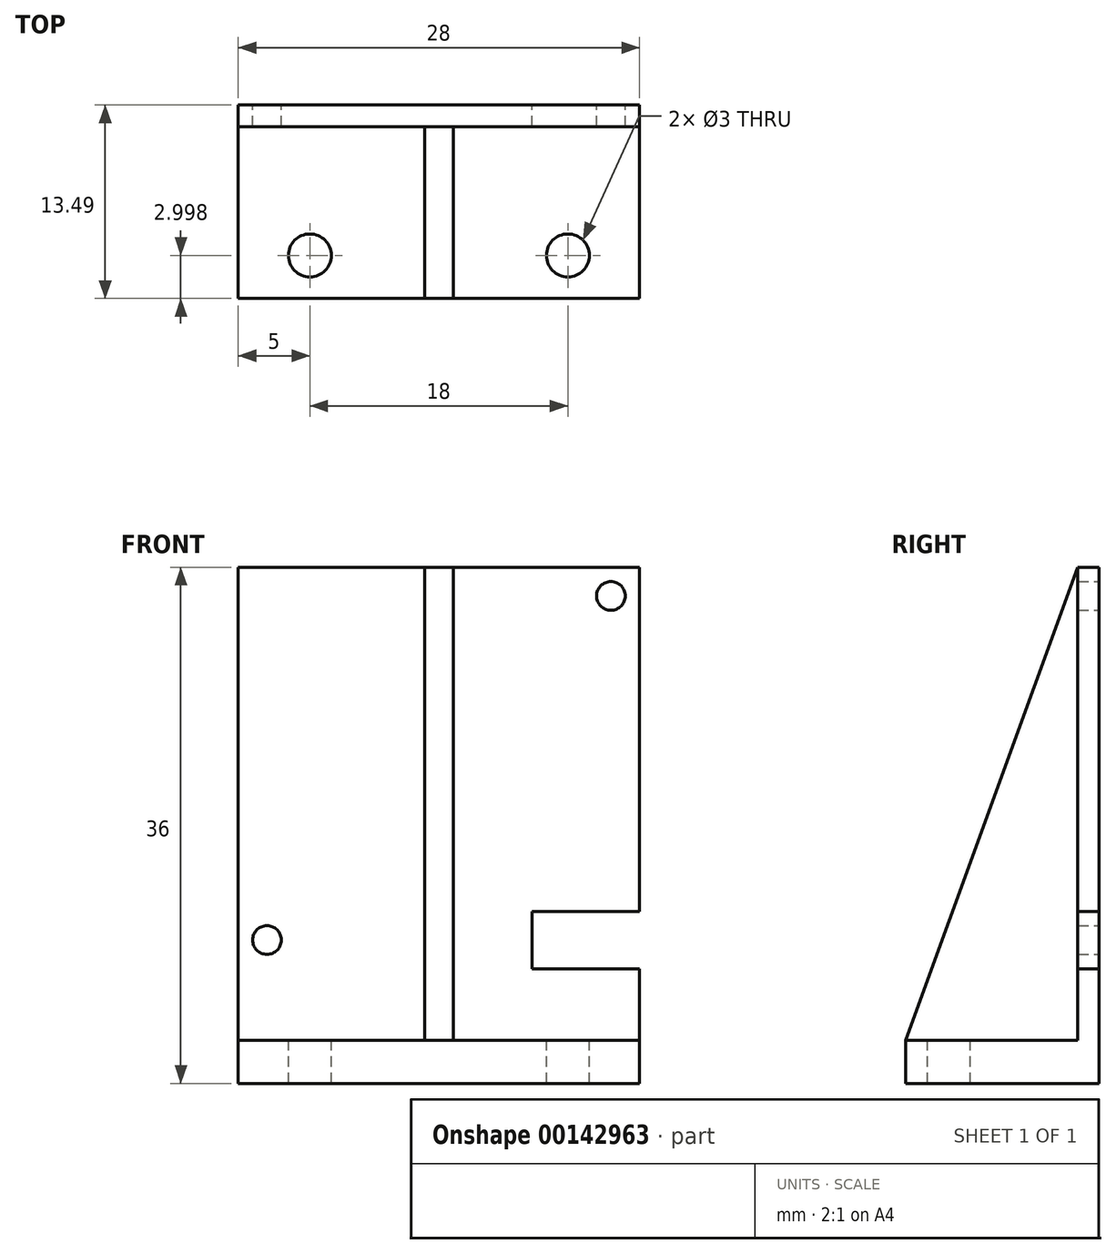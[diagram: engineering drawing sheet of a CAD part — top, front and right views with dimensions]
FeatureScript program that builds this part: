
annotation { "Feature Type Name" : "Feature", "Feature Type Description" : "" }
export const myFeature = defineFeature(function(context is Context, id is Id, definition is map)
    precondition{}
    {
        {
            var Q0;
            Q0=qCreatedBy(makeId("Front.planeOp"),FACE);
            var sketch = newSketch(context, id + "F0", { "sketchPlane" : qUnion([Q0])});
            skLineSegment(sketch, "E0.bottom", {"start": v(14, 16.5) * mm, "end": v(-14, 16.5) * mm});
            skLineSegment(sketch, "E0.top", {"start": v(14, -16.5) * mm, "end": v(-14, -16.5) * mm});
            skLineSegment(sketch, "E0.left", {"start": v(14, 16.5) * mm, "end": v(14, -7.5) * mm});
            skLineSegment(sketch, "E0.right", {"start": v(-14, 16.5) * mm, "end": v(-14, -16.5) * mm});
            skPoint(sketch, "E0.middle", {"position": v(0, 0) * mm});
            skLineSegment(sketch, "E1.bottom", {"start": v(14, -16.5) * mm, "end": v(6.5, -16.5) * mm});
            skLineSegment(sketch, "E1.top", {"start": v(14, -7.5) * mm, "end": v(6.5, -7.5) * mm});
            skLineSegment(sketch, "E1.left", {"start": v(14, -16.5) * mm, "end": v(14, -11.5) * mm});
            skLineSegment(sketch, "E1.right", {"start": v(6.5, -11.5) * mm, "end": v(6.5, -7.5) * mm});
            skLineSegment(sketch, "E2", {"start": v(6.5, -11.5) * mm, "end": v(14, -11.5) * mm});
            skPoint(sketch, "E3.orphan", {"position": v(-14, -11.5) * mm});
            skLineSegment(sketch, "E4.trimOffspring", {"start": v(14, -11.5) * mm, "end": v(14, -16.5) * mm});
            skCircle(sketch, "E5", {"center": v(12, 14.5) * mm, "radius": 1 * mm});
            skCircle(sketch, "E6", {"center": v(-12, -9.5) * mm, "radius": 1 * mm});
            skSolve(sketch);
        }
        {
            var Q0;
            Q0=makeQuery(id+"F0.imprint","IMPRINT",FACE,{"disambiguationData":[TD([[makeQuery(id+"F0.imprint","IMPRINT",EDGE,{"derivedFrom":sQuery(id+"F0.wireOp",EDGE,"E0.bottom")}),1.0]])]});
            extrude(context, id + "F1", {"entities" : qUnion([Q0]), "depth" : 1.5 * mm});
        }
        {
            var Q0;
            Q0=makeQuery(id+"F1.opExtrude","SWEPT_FACE",FACE,{"disambiguationData":[OSD([sQuery(id+"F0.wireOp",EDGE,"E0.top")])]});
            var sketch = newSketch(context, id + "F2", { "sketchPlane" : qUnion([Q0])});
            skLineSegment(sketch, "E7.bottom", {"start": v(-14, 0) * mm, "end": v(14, 0) * mm});
            skLineSegment(sketch, "E7.top", {"start": v(-14, 13.5) * mm, "end": v(14, 13.5) * mm});
            skLineSegment(sketch, "E7.left", {"start": v(-14, 0) * mm, "end": v(-14, 13.5) * mm});
            skLineSegment(sketch, "E7.right", {"start": v(14, 0) * mm, "end": v(14, 13.5) * mm});
            skCircle(sketch, "E8", {"center": v(-9, 10.5) * mm, "radius": 1.5 * mm});
            skCircle(sketch, "E9", {"center": v(9, 10.5) * mm, "radius": 1.5 * mm});
            skSolve(sketch);
        }
        {
            var Q0;
            Q0 = qSketchRegion(id + "F2", true);
            extrude(context, id + "F3", {"entities" : qUnion([Q0]), "operationType" : NewBodyOperationType.ADD, "depth" : 3 * mm});
        }
        {
            var Q0;
            Q0=makeQuery(id+"F3.boolean.opBoolean","MERGE",FACE,{"derivedFrom":[makeQuery(id+"F1.opExtrude","SWEPT_FACE",FACE,{"disambiguationData":[OSD([sQuery(id+"F0.wireOp",EDGE,"E1.left")])]}),makeQuery(id+"F3.opExtrude","SWEPT_FACE",FACE,{"disambiguationData":[OSD([sQuery(id+"F2.wireOp",EDGE,"E7.right")])]})]});
            var sketch = newSketch(context, id + "F4", { "sketchPlane" : qUnion([Q0])});
            skLineSegment(sketch, "E10.0", {"start": v(-1.5, 16.5) * mm, "end": v(-1.5, -7.5) * mm});
            skLineSegment(sketch, "E11", {"start": v(-1.5, 16.5) * mm, "end": v(-13.5, -16.5) * mm});
            skLineSegment(sketch, "E12", {"start": v(-13.5, -16.5) * mm, "end": v(-1.5, -16.5) * mm});
            skLineSegment(sketch, "E13", {"start": v(-1.5, -16.5) * mm, "end": v(-1.5, 16.5) * mm});
            skSolve(sketch);
        }
        {
            var Q0;
            Q0 = qSketchRegion(id + "F4", true);
            extrude(context, id + "F5", {"entities" : qUnion([Q0]), "depth" : 2 * mm, "symmetric" : true});
        }
        {
            var Q0;
            Q0=makeQuery(id+"F5.opExtrude","SWEPT_BODY",BODY,{"disambiguationData":[OSD([sQuery(id+"F4.wireOp",EDGE,"E11"),sQuery(id+"F4.wireOp",EDGE,"E12"),sQuery(id+"F4.wireOp",EDGE,"E13")])]});
            transform(context, id + "F6", {"entities" : qUnion([Q0]), "transformType" : TransformType.TRANSLATION_3D, "dx" : -14 * mm, "dy" : 0 * mm, "dz" : 0 * mm, "makeCopy" : false});
        }
    });
